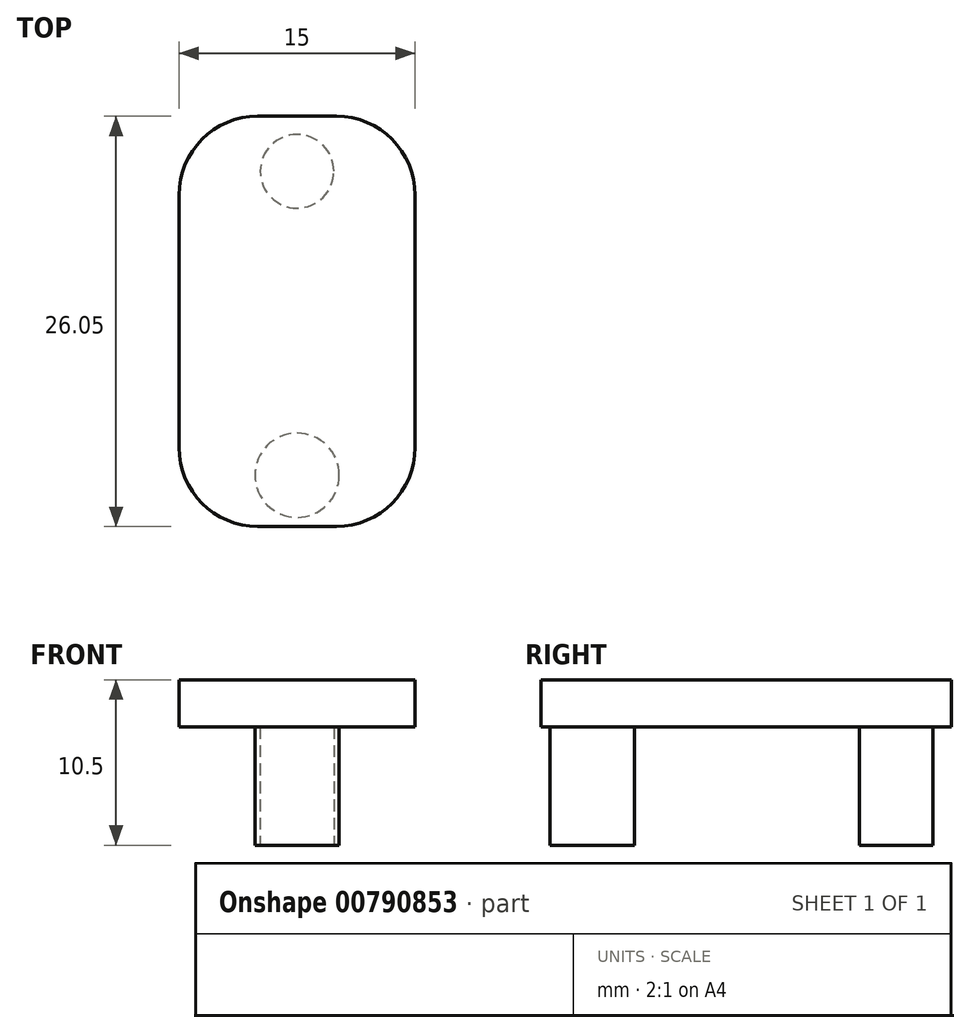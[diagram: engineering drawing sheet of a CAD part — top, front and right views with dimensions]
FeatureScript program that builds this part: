
annotation { "Feature Type Name" : "Feature", "Feature Type Description" : "" }
export const myFeature = defineFeature(function(context is Context, id is Id, definition is map)
    precondition{}
    {
        {
            var Q0;
            Q0=qCreatedBy(makeId("Top.planeOp"),FACE);
            var sketch = newSketch(context, id + "F0", { "sketchPlane" : qUnion([Q0])});
            skCircle(sketch, "E0", {"center": v(0, 0) * mm, "radius": 2.67 * mm});
            skCircle(sketch, "E1", {"center": v(0, 19.3) * mm, "radius": 2.34 * mm});
            skSolve(sketch);
        }
        {
            var Q0;
            Q0 = qSketchRegion(id + "F0", true);
            extrude(context, id + "F1", {"entities" : qUnion([Q0]), "depth" : 7.5 * mm, "offsetDistance" : 25 * mm});
        }
        {
            var Q0;
            Q0=makeQuery(id+"F1.opExtrude","CAP_FACE",FACE,{"disambiguationData":[OSD([sQuery(id+"F0.wireOp",EDGE,"E1")])],"isStart":false});
            var sketch = newSketch(context, id + "F2", { "sketchPlane" : qUnion([Q0])});
            skLineSegment(sketch, "E2.bottom", {"start": v(-7.5, 3.25) * mm, "end": v(7.5, 3.25) * mm});
            skLineSegment(sketch, "E2.top", {"start": v(-7.5, -3.25) * mm, "end": v(7.5, -3.25) * mm});
            skLineSegment(sketch, "E2.left", {"start": v(-7.5, 3.25) * mm, "end": v(-7.5, -3.25) * mm});
            skLineSegment(sketch, "E2.right", {"start": v(7.5, 3.25) * mm, "end": v(7.5, -3.25) * mm});
            skPoint(sketch, "E2.middle", {"position": v(0, 0) * mm});
            skLineSegment(sketch, "E3.bottom", {"start": v(-7.5, 15.8) * mm, "end": v(7.5, 15.8) * mm});
            skLineSegment(sketch, "E3.top", {"start": v(-7.5, 22.8) * mm, "end": v(7.5, 22.8) * mm});
            skLineSegment(sketch, "E3.left", {"start": v(-7.5, 15.8) * mm, "end": v(-7.5, 22.8) * mm});
            skLineSegment(sketch, "E3.right", {"start": v(7.5, 15.8) * mm, "end": v(7.5, 22.8) * mm});
            skPoint(sketch, "E3.middle", {"position": v(0, 19.3) * mm});
            skLineSegment(sketch, "E4", {"start": v(-7.5, 15.8) * mm, "end": v(-7.5, 3.25) * mm});
            skLineSegment(sketch, "E5", {"start": v(7.5, 15.8) * mm, "end": v(7.5, 3.25) * mm});
            skSolve(sketch);
        }
        {
            var Q0;
            Q0=makeQuery(id+"F2.imprint","IMPRINT",FACE,{"disambiguationData":[TD([[makeQuery(id+"F2.imprint","IMPRINT",EDGE,{"derivedFrom":makeQuery(id+"F1.opExtrude","CAP_EDGE",EDGE,{"disambiguationData":[OSD([sQuery(id+"F0.wireOp",EDGE,"E1")])],"isStart":false})}),-1.0]])]});
            var Q1;
            {var subQ0=sQuery(id+"F2.wireOp",EDGE,"TZnfkHZf-DKkp-xptn-AsGC-FlYiCB8cDqTM");Q1=makeQuery(id+"F2.imprint","IMPRINT",FACE,{"disambiguationData":[TD([[makeQuery(id+"F2.imprint","IMPRINT",EDGE,{"derivedFrom":subQ0}),-1.0]])]});}
            var Q2;
            {var subQ0=sQuery(id+"F2.wireOp",EDGE,"XSsqlgjZ-LNJ9-Avoh-l53S-mxeqoTWxBHOC");var subQ1=makeQuery(id+"F2.imprint","INTERSECT",VERTEX,{"derivedFrom":[subQ0,sQuery(id+"F2.wireOp",EDGE,"TZnfkHZf-DKkp-xptn-AsGC-FlYiCB8cDqTM")]});Q2=makeQuery(id+"F2.imprint","IMPRINT",FACE,{"disambiguationData":[TD([[makeQuery(id+"F2.imprint","IMPRINT",EDGE,{"disambiguationData":[TD([[subQ1,1.0]])],"derivedFrom":subQ0}),1.0]])]});}
            var Q3;
            Q3=makeQuery(id+"F2.imprint","IMPRINT",FACE,{"disambiguationData":[TD([[makeQuery(id+"F2.imprint","IMPRINT",EDGE,{"derivedFrom":makeQuery(id+"F1.opExtrude","CAP_EDGE",EDGE,{"disambiguationData":[OSD([sQuery(id+"F0.wireOp",EDGE,"E1")])],"isStart":false})}),1.0]])]});
            var Q4;
            Q4=makeQuery(id+"F2.imprint","IMPRINT",FACE,{"disambiguationData":[TD([[makeQuery(id+"F2.imprint","IMPRINT",EDGE,{"derivedFrom":sQuery(id+"F2.wireOp",EDGE,"E2.bottom")}),1.0]])]});
            var Q5;
            Q5=makeQuery(id+"F2.imprint","IMPRINT",FACE,{"disambiguationData":[TD([[makeQuery(id+"F2.imprint","IMPRINT",EDGE,{"derivedFrom":sQuery(id+"F2.wireOp",EDGE,"E2.bottom")}),-1.0]])]});
            extrude(context, id + "F3", {"entities" : qUnion([Q0, Q1, Q2, Q3, Q4, Q5]), "depth" : 3 * mm, "offsetDistance" : 25 * mm});
        }
        {
            var Q0;
            Q0=makeQuery(id+"F3.opExtrude","SWEPT_EDGE",EDGE,{"disambiguationData":[OSD([sQuery(id+"F2.wireOp",EDGE,"E2.top"),sQuery(id+"F2.wireOp",EDGE,"E2.left")])]});
            var Q1;
            Q1=makeQuery(id+"F3.opExtrude","SWEPT_EDGE",EDGE,{"disambiguationData":[OSD([sQuery(id+"F2.wireOp",EDGE,"E2.top"),sQuery(id+"F2.wireOp",EDGE,"E2.right")])]});
            var Q2;
            Q2=makeQuery(id+"F3.opExtrude","SWEPT_EDGE",EDGE,{"disambiguationData":[OSD([sQuery(id+"F2.wireOp",EDGE,"E3.top"),sQuery(id+"F2.wireOp",EDGE,"E3.right")])]});
            var Q3;
            Q3=makeQuery(id+"F3.opExtrude","SWEPT_EDGE",EDGE,{"disambiguationData":[OSD([sQuery(id+"F2.wireOp",EDGE,"E3.top"),sQuery(id+"F2.wireOp",EDGE,"E3.left")])]});
            fillet(context, id + "F4", {"entities" : qUnion([Q0, Q1, Q2, Q3]), "tangentPropagation" : true, "radius" : 5 * mm, "defaultsChanged" : false, "vertexSettings" : [], "allowEdgeOverflow" : false});
        }
    });
